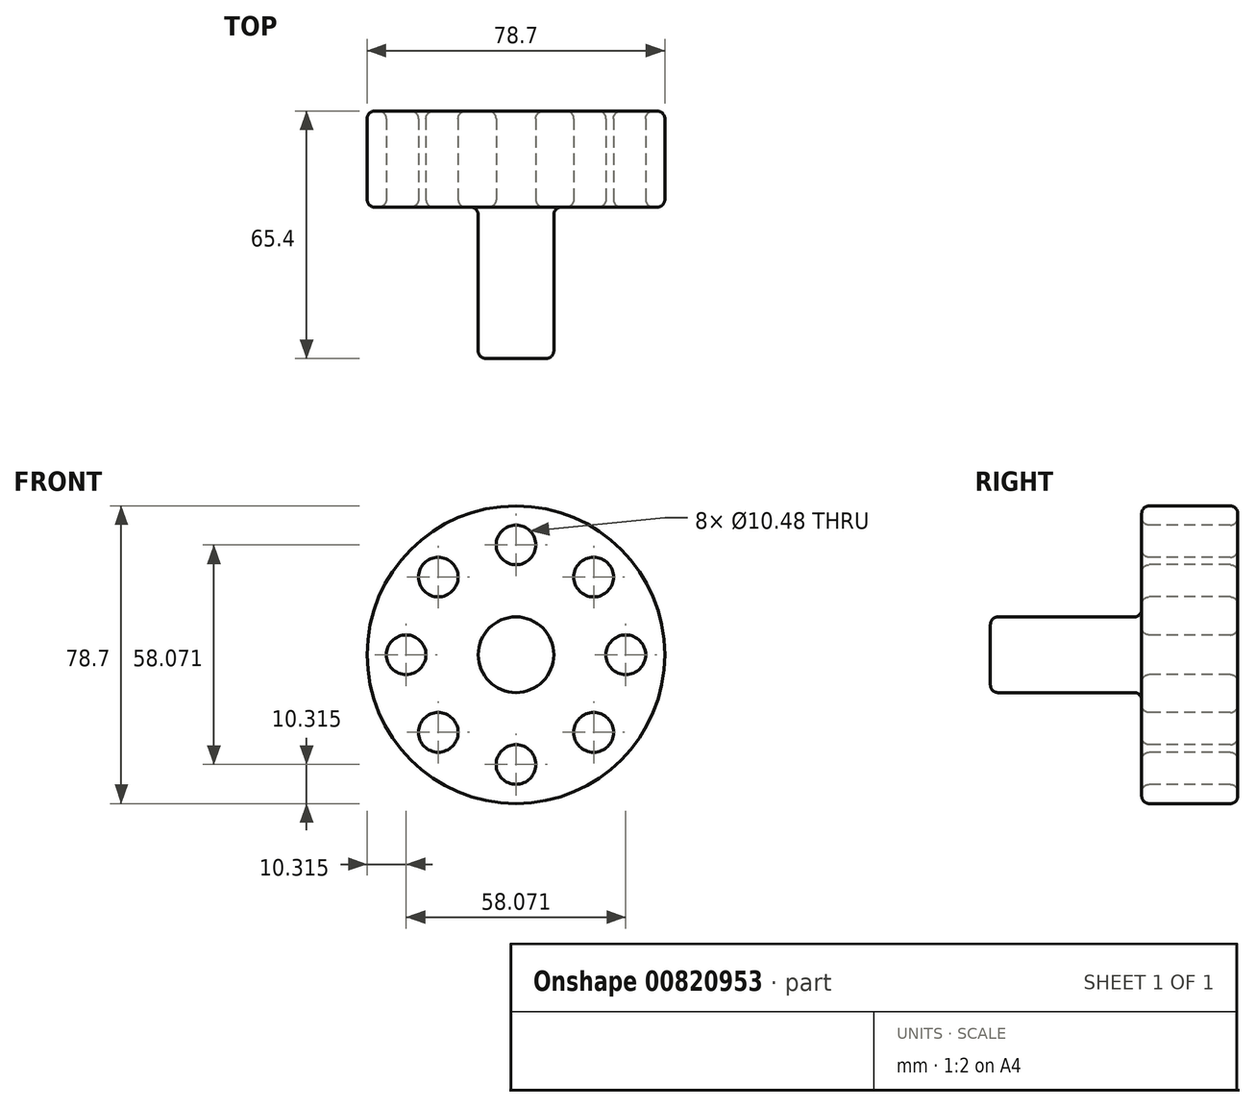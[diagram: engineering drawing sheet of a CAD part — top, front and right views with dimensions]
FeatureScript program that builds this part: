
annotation { "Feature Type Name" : "Feature", "Feature Type Description" : "" }
export const myFeature = defineFeature(function(context is Context, id is Id, definition is map)
    precondition{}
    {
        {
            var Q0;
            Q0=qCreatedBy(makeId("Front.planeOp"),FACE);
            var sketch = newSketch(context, id + "F0", { "sketchPlane" : qUnion([Q0])});
            skCircle(sketch, "E0", {"center": v(0, 0) * mm, "radius": 39.35 * mm});
            skSolve(sketch);
        }
        {
            var Q0;
            Q0=makeQuery(id+"F0.imprint","IMPRINT",FACE,{"disambiguationData":[TD([[makeQuery(id+"F0.imprint","IMPRINT",EDGE,{"derivedFrom":sQuery(id+"F0.wireOp",EDGE,"E0")}),1.0]])]});
            extrude(context, id + "F1", {"entities" : qUnion([Q0]), "depth" : 25.4 * mm, "offsetDistance" : 25.4 * mm});
        }
        {
            var Q0;
            Q0=makeQuery(id+"F1.opExtrude","CAP_FACE",FACE,{"disambiguationData":[OSD([sQuery(id+"F0.wireOp",EDGE,"E0")])],"isStart":false});
            var sketch = newSketch(context, id + "F2", { "sketchPlane" : qUnion([Q0])});
            skCircle(sketch, "E1", {"center": v(0, 29.04) * mm, "radius": 5.24 * mm});
            skCircle(sketch, "E2.1.0", {"center": v(-20.53, 20.53) * mm, "radius": 5.24 * mm});
            skCircle(sketch, "E2.2.0", {"center": v(-29.04, 0) * mm, "radius": 5.24 * mm});
            skCircle(sketch, "E2.3.0", {"center": v(-20.53, -20.53) * mm, "radius": 5.24 * mm});
            skCircle(sketch, "E2.4.0", {"center": v(0, -29.04) * mm, "radius": 5.24 * mm});
            skCircle(sketch, "E2.5.0", {"center": v(20.53, -20.53) * mm, "radius": 5.24 * mm});
            skCircle(sketch, "E2.6.0", {"center": v(29.04, 0) * mm, "radius": 5.24 * mm});
            skCircle(sketch, "E2.7.0", {"center": v(20.53, 20.53) * mm, "radius": 5.24 * mm});
            skPoint(sketch, "E2.center", {"position": v(0, 0) * mm});
            skSolve(sketch);
        }
        {
            var Q0;
            Q0=makeQuery(id+"F2.imprint","IMPRINT",FACE,{"disambiguationData":[TD([[makeQuery(id+"F2.imprint","IMPRINT",EDGE,{"derivedFrom":sQuery(id+"F2.wireOp",EDGE,"E1")}),1.0]])]});
            var Q1;
            Q1=makeQuery(id+"F2.imprint","IMPRINT",FACE,{"disambiguationData":[TD([[makeQuery(id+"F2.imprint","IMPRINT",EDGE,{"derivedFrom":sQuery(id+"F2.wireOp",EDGE,"E2.7.0")}),1.0]])]});
            var Q2;
            Q2=makeQuery(id+"F2.imprint","IMPRINT",FACE,{"disambiguationData":[TD([[makeQuery(id+"F2.imprint","IMPRINT",EDGE,{"derivedFrom":sQuery(id+"F2.wireOp",EDGE,"E2.6.0")}),1.0]])]});
            var Q3;
            Q3=makeQuery(id+"F2.imprint","IMPRINT",FACE,{"disambiguationData":[TD([[makeQuery(id+"F2.imprint","IMPRINT",EDGE,{"derivedFrom":sQuery(id+"F2.wireOp",EDGE,"E2.5.0")}),1.0]])]});
            var Q4;
            Q4=makeQuery(id+"F2.imprint","IMPRINT",FACE,{"disambiguationData":[TD([[makeQuery(id+"F2.imprint","IMPRINT",EDGE,{"derivedFrom":sQuery(id+"F2.wireOp",EDGE,"E2.4.0")}),1.0]])]});
            var Q5;
            Q5=makeQuery(id+"F2.imprint","IMPRINT",FACE,{"disambiguationData":[TD([[makeQuery(id+"F2.imprint","IMPRINT",EDGE,{"derivedFrom":sQuery(id+"F2.wireOp",EDGE,"E2.3.0")}),1.0]])]});
            var Q6;
            Q6=makeQuery(id+"F2.imprint","IMPRINT",FACE,{"disambiguationData":[TD([[makeQuery(id+"F2.imprint","IMPRINT",EDGE,{"derivedFrom":sQuery(id+"F2.wireOp",EDGE,"E2.2.0")}),1.0]])]});
            var Q7;
            Q7=makeQuery(id+"F2.imprint","IMPRINT",FACE,{"disambiguationData":[TD([[makeQuery(id+"F2.imprint","IMPRINT",EDGE,{"derivedFrom":sQuery(id+"F2.wireOp",EDGE,"E2.1.0")}),1.0]])]});
            extrude(context, id + "F3", {"entities" : qUnion([Q0, Q1, Q2, Q3, Q4, Q5, Q6, Q7]), "operationType" : NewBodyOperationType.REMOVE, "oppositeDirection" : true, "depth" : 28 * mm, "offsetDistance" : 25 * mm});
        }
        {
            var Q0;
            Q0=makeQuery(id+"F1.opExtrude","CAP_FACE",FACE,{"disambiguationData":[OSD([sQuery(id+"F0.wireOp",EDGE,"E0")])],"isStart":false});
            var sketch = newSketch(context, id + "F4", { "sketchPlane" : qUnion([Q0])});
            skCircle(sketch, "E3", {"center": v(0, 0) * mm, "radius": 10 * mm});
            skSolve(sketch);
        }
        {
            var Q0;
            Q0=makeQuery(id+"F4.imprint","IMPRINT",FACE,{"disambiguationData":[TD([[makeQuery(id+"F4.imprint","IMPRINT",EDGE,{"derivedFrom":sQuery(id+"F4.wireOp",EDGE,"E3")}),1.0]])]});
            extrude(context, id + "F5", {"entities" : qUnion([Q0]), "operationType" : NewBodyOperationType.ADD, "depth" : 40 * mm, "offsetDistance" : 25 * mm});
        }
        {
            var Q0;
            Q0=makeQuery(id+"F5.opExtrude","CAP_FACE",FACE,{"disambiguationData":[OSD([sQuery(id+"F4.wireOp",EDGE,"E3")])],"isStart":false});
            fillet(context, id + "F6", {"entities" : qUnion([Q0]), "radius" : 2 * mm, "tangentPropagation" : true, "allowEdgeOverflow" : false});
        }
        {
            var Q0;
            Q0=makeQuery(id+"F1.opExtrude","SWEPT_FACE",FACE,{"disambiguationData":[OSD([sQuery(id+"F0.wireOp",EDGE,"E0")])]});
            fillet(context, id + "F7", {"entities" : qUnion([Q0]), "radius" : 2 * mm, "tangentPropagation" : true, "allowEdgeOverflow" : false});
        }
        {
            var Q0;
            Q0=makeQuery(id+"F1.opExtrude","CAP_FACE",FACE,{"disambiguationData":[OSD([sQuery(id+"F0.wireOp",EDGE,"E0")])],"isStart":false});
            fillet(context, id + "F8", {"entities" : qUnion([Q0]), "radius" : 2 * mm, "tangentPropagation" : true, "allowEdgeOverflow" : false});
        }
        {
            var Q0;
            Q0=makeQuery(id+"F1.opExtrude","CAP_FACE",FACE,{"disambiguationData":[OSD([sQuery(id+"F0.wireOp",EDGE,"E0")])],"isStart":true});
            fillet(context, id + "F9", {"entities" : qUnion([Q0]), "radius" : 2 * mm, "tangentPropagation" : true, "allowEdgeOverflow" : false});
        }
    });
